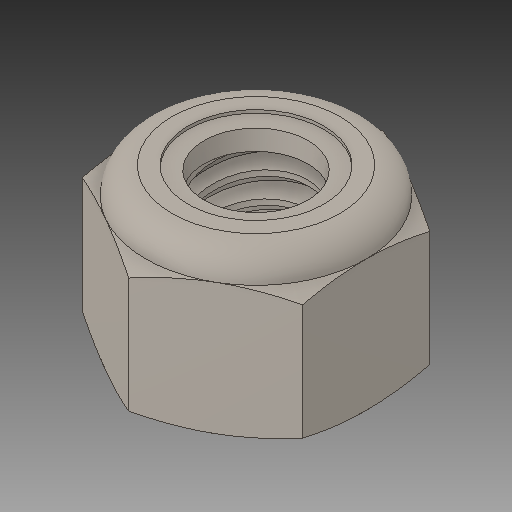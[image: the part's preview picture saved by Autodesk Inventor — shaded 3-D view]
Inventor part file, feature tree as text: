
AUTODESK INVENTOR PART (.ipt)
format: ipt  version: 2018 (Build 220112000, 112)  size: 302,592 bytes
history: native  units: in
note: dims shown in document units (in); Inventor stores cm internally (conversion verified against a paired STEP export)
features: other x1, revolve x1
ambient origin geometry x8: Origin, YZ Plane, XZ Plane, XY Plane, X Axis, Y Axis, Z Axis, Center Point
bodies: Solid1 (feature_tree), Solid2 (feature_tree)
feature tree (2):
  other  "Cut-Revolve4"
  revolve  "Revolve2"  [1 undecoded]
note: 1 required parameter value undecoded (feature->parameter linkage not recoverable at this tier; creation-order binding heuristic only, values carry confidence <= 0.55)
